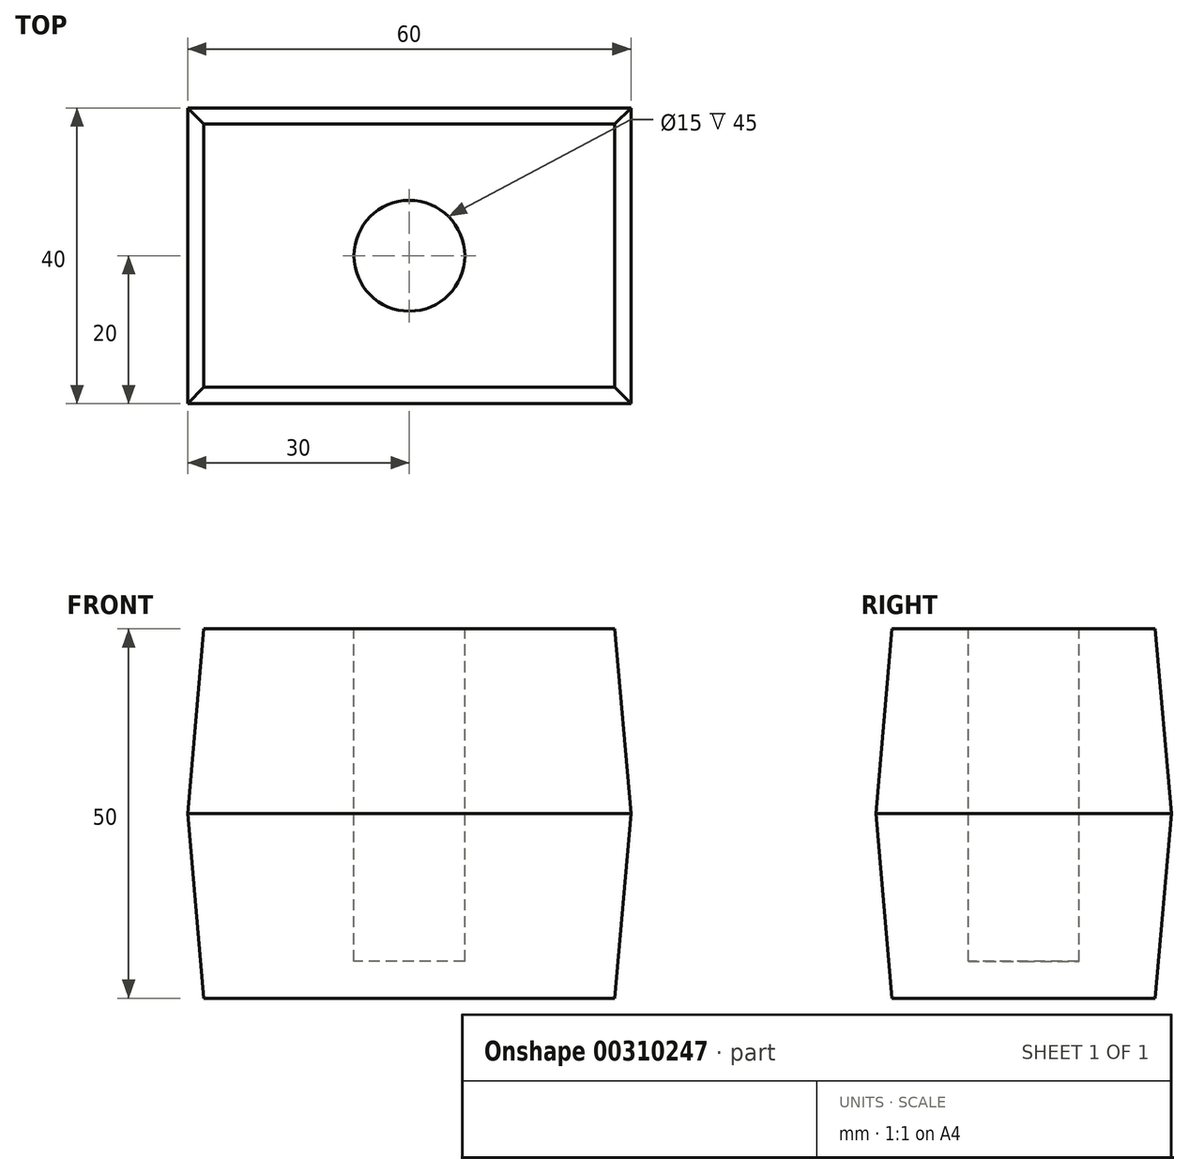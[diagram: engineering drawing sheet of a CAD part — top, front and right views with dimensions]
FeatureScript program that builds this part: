
annotation { "Feature Type Name" : "Feature", "Feature Type Description" : "" }
export const myFeature = defineFeature(function(context is Context, id is Id, definition is map)
    precondition{}
    {
        {
            var Q0;
            Q0=qCreatedBy(makeId("Top.planeOp"),FACE);
            var sketch = newSketch(context, id + "F0", { "sketchPlane" : qUnion([Q0])});
            skLineSegment(sketch, "E0.bottom", {"start": v(0, 0) * mm, "end": v(60, 0) * mm});
            skLineSegment(sketch, "E0.top", {"start": v(0, 40) * mm, "end": v(60, 40) * mm});
            skLineSegment(sketch, "E0.left", {"start": v(0, 0) * mm, "end": v(0, 40) * mm});
            skLineSegment(sketch, "E0.right", {"start": v(60, 0) * mm, "end": v(60, 40) * mm});
            skSolve(sketch);
        }
        {
            var Q0;
            Q0 = qSketchRegion(id + "F0", true);
            extrude(context, id + "F1", {"entities" : qUnion([Q0]), "depth" : 25 * mm, "hasDraft" : true, "draftAngle" : 5 * degree, "draftPullDirection" : true, "hasSecondDirection" : true, "secondDirectionOppositeDirection" : true, "secondDirectionDepth" : 25 * mm, "hasSecondDirectionDraft" : true, "secondDirectionDraftAngle" : 5 * degree, "secondDirectionDraftPullDirection" : true});
        }
        {
            var Q0;
            Q0=makeQuery(id+"F1.opExtrude","CAP_FACE",FACE,{"disambiguationData":[OSD([sQuery(id+"F0.wireOp",EDGE,"E0.bottom"),sQuery(id+"F0.wireOp",EDGE,"E0.top"),sQuery(id+"F0.wireOp",EDGE,"E0.left"),sQuery(id+"F0.wireOp",EDGE,"E0.right")])],"isStart":false});
            var sketch = newSketch(context, id + "F2", { "sketchPlane" : qUnion([Q0])});
            skCircle(sketch, "E1", {"center": v(30, 20) * mm, "radius": 7.5 * mm});
            skLineSegment(sketch, "E2", {"start": v(2.19, 2.19) * mm, "end": v(57.81, 37.81) * mm, "construction": true});
            skSolve(sketch);
        }
        {
            var Q0;
            Q0 = qSketchRegion(id + "F2", true);
            extrude(context, id + "F3", {"entities" : qUnion([Q0]), "operationType" : NewBodyOperationType.REMOVE, "oppositeDirection" : true, "depth" : 45 * mm});
        }
    });
